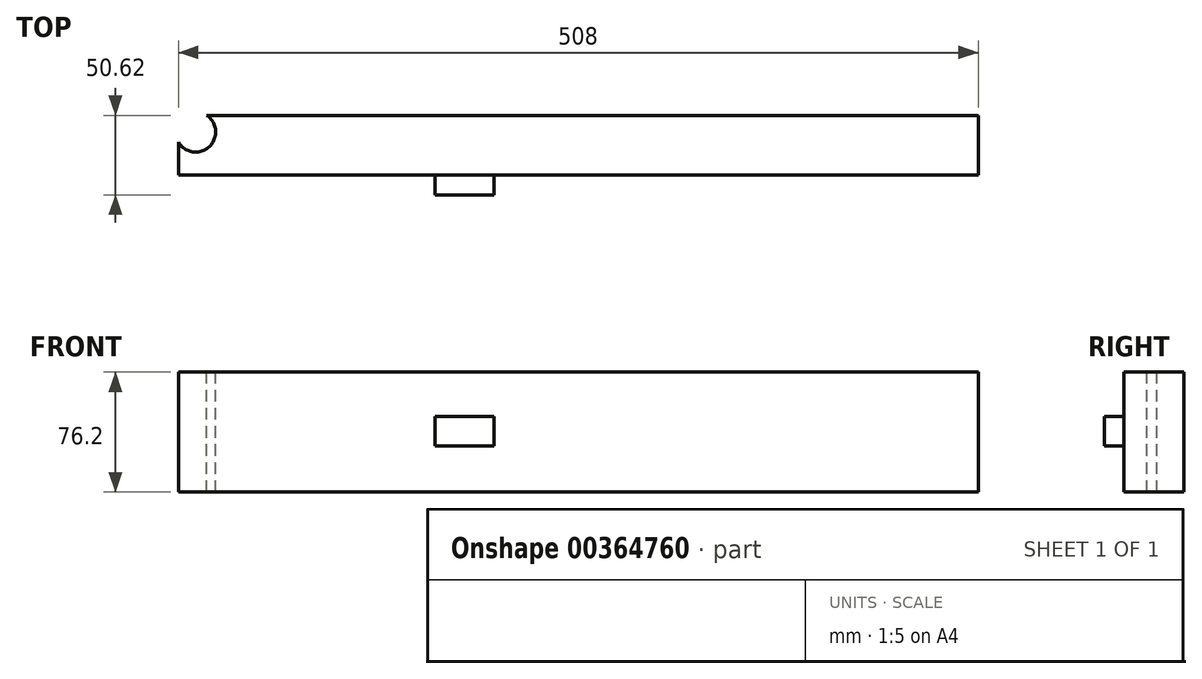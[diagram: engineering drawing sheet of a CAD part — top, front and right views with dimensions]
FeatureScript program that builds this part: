
annotation { "Feature Type Name" : "Feature", "Feature Type Description" : "" }
export const myFeature = defineFeature(function(context is Context, id is Id, definition is map)
    precondition{}
    {
        {
            var Q0;
            Q0=qCreatedBy(makeId("Top.planeOp"),FACE);
            var sketch = newSketch(context, id + "F0", { "sketchPlane" : qUnion([Q0])});
            skLineSegment(sketch, "E0.bottom", {"start": v(-21.23, 17.63) * mm, "end": v(486.77, 17.63) * mm});
            skLineSegment(sketch, "E0.top", {"start": v(-21.23, -20.29) * mm, "end": v(486.77, -20.29) * mm});
            skLineSegment(sketch, "E0.left", {"start": v(-21.23, 17.63) * mm, "end": v(-21.23, -20.29) * mm});
            skLineSegment(sketch, "E0.right", {"start": v(486.77, 17.63) * mm, "end": v(486.77, -20.29) * mm});
            skCircle(sketch, "E1", {"center": v(-10.24, 7.02) * mm, "radius": 12.7 * mm});
            skSolve(sketch);
        }
        {
            var Q0;
            {var subQ1=sQuery(id+"F0.wireOp",EDGE,"E0.top");Q0=makeQuery(id+"F0.imprint","IMPRINT",FACE,{"disambiguationData":[TD([[makeQuery(id+"F0.imprint","IMPRINT",EDGE,{"derivedFrom":subQ1}),1.0]])]});}
            extrude(context, id + "F1", {"entities" : qUnion([Q0]), "oppositeDirection" : true, "depth" : 76.2 * mm});
        }
        {
            var Q0;
            Q0=makeQuery(id+"F1.opExtrude","SWEPT_FACE",FACE,{"disambiguationData":[OSD([sQuery(id+"F0.wireOp",EDGE,"E0.top")])]});
            var sketch = newSketch(context, id + "F2", { "sketchPlane" : qUnion([Q0])});
            skLineSegment(sketch, "E2.bottom", {"start": v(141.86, -28.27) * mm, "end": v(179.2, -28.27) * mm});
            skLineSegment(sketch, "E2.top", {"start": v(141.86, -46.81) * mm, "end": v(179.2, -46.81) * mm});
            skLineSegment(sketch, "E2.left", {"start": v(141.86, -28.27) * mm, "end": v(141.86, -46.81) * mm});
            skLineSegment(sketch, "E2.right", {"start": v(179.2, -28.27) * mm, "end": v(179.2, -46.81) * mm});
            skSolve(sketch);
        }
        {
            var Q0;
            Q0=makeQuery(id+"F2.imprint","IMPRINT",FACE,{"disambiguationData":[TD([[makeQuery(id+"F2.imprint","IMPRINT",EDGE,{"derivedFrom":sQuery(id+"F2.wireOp",EDGE,"E2.bottom")}),-1.0]])]});
            extrude(context, id + "F3", {"entities" : qUnion([Q0]), "operationType" : NewBodyOperationType.ADD, "depth" : 12.7 * mm});
        }
    });
